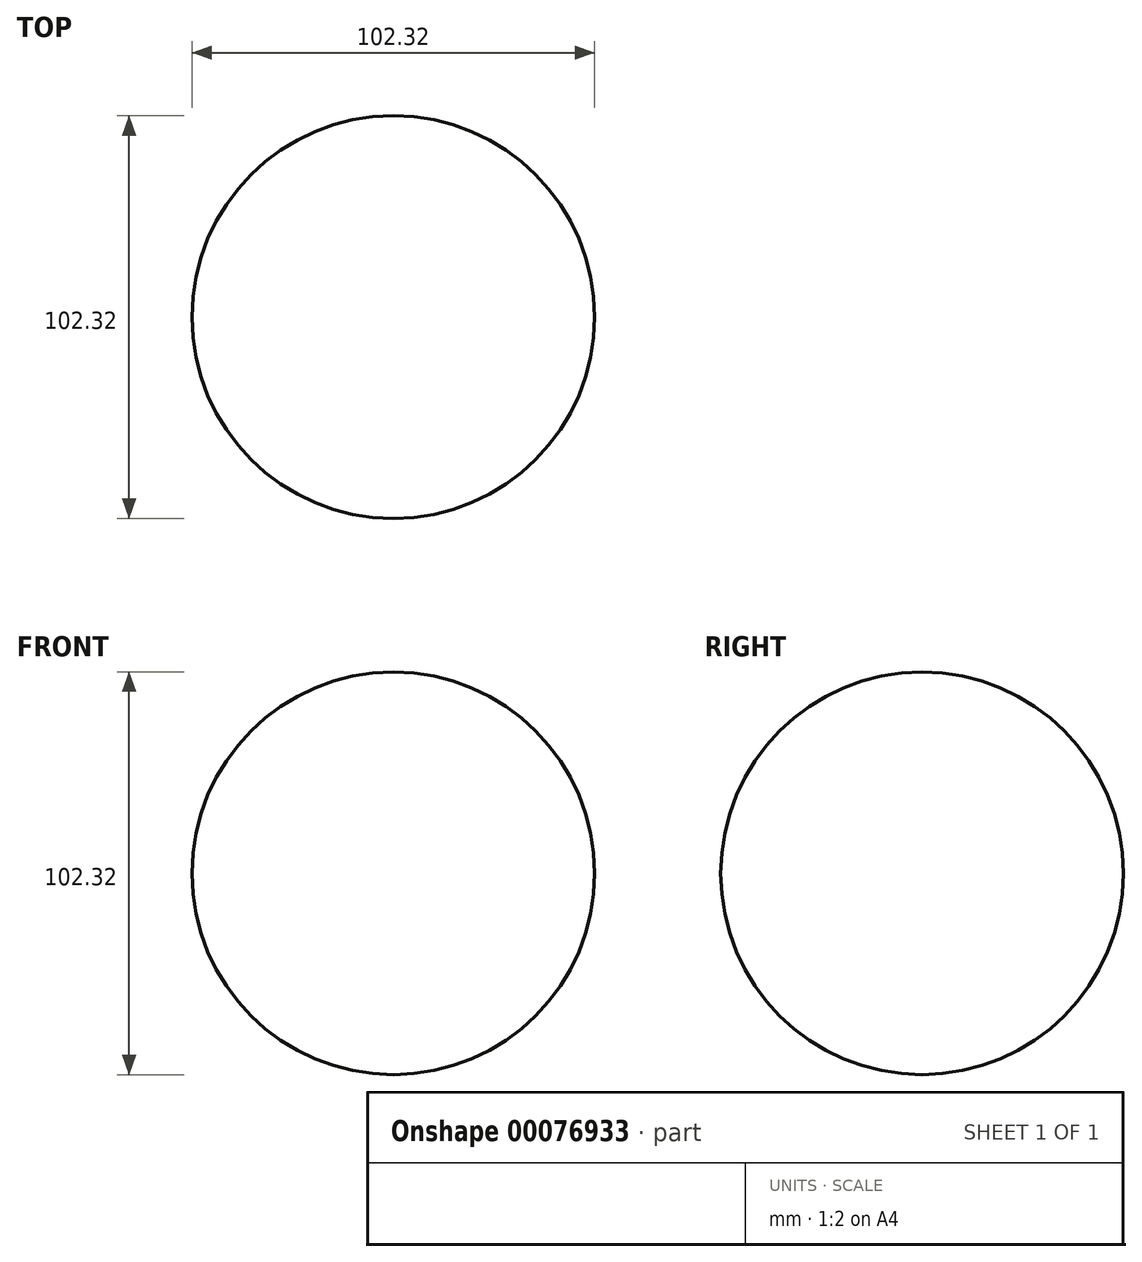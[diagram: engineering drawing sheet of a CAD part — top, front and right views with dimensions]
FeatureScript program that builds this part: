
annotation { "Feature Type Name" : "Feature", "Feature Type Description" : "" }
export const myFeature = defineFeature(function(context is Context, id is Id, definition is map)
    precondition{}
    {
        {
            var Q0;
            Q0=qCreatedBy(makeId("Top.planeOp"),FACE);
            var sketch = newSketch(context, id + "F0", { "sketchPlane" : qUnion([Q0])});
            skArc(sketch, "E0", {"start": v(0, -51.16) * mm, "mid": v(51.16, 0) * mm, "end": v(0, 51.16) * mm});
            skLineSegment(sketch, "E1", {"start": v(0, 51.16) * mm, "end": v(0, -51.16) * mm});
            skSolve(sketch);
        }
        {
            var Q0;
            Q0=makeQuery(id+"F0.imprint","IMPRINT",FACE,{"disambiguationData":[TD([[makeQuery(id+"F0.imprint","IMPRINT",EDGE,{"derivedFrom":sQuery(id+"F0.wireOp",EDGE,"E0")}),1.0]])]});
            var Q1;
            Q1=sQuery(id+"F0.wireOp",EDGE,"E1");
            revolve(context, id + "F1", {"entities" : qUnion([Q0]), "axis" : qUnion([Q1]), "revolveType" : RevolveType.FULL});
        }
    });
